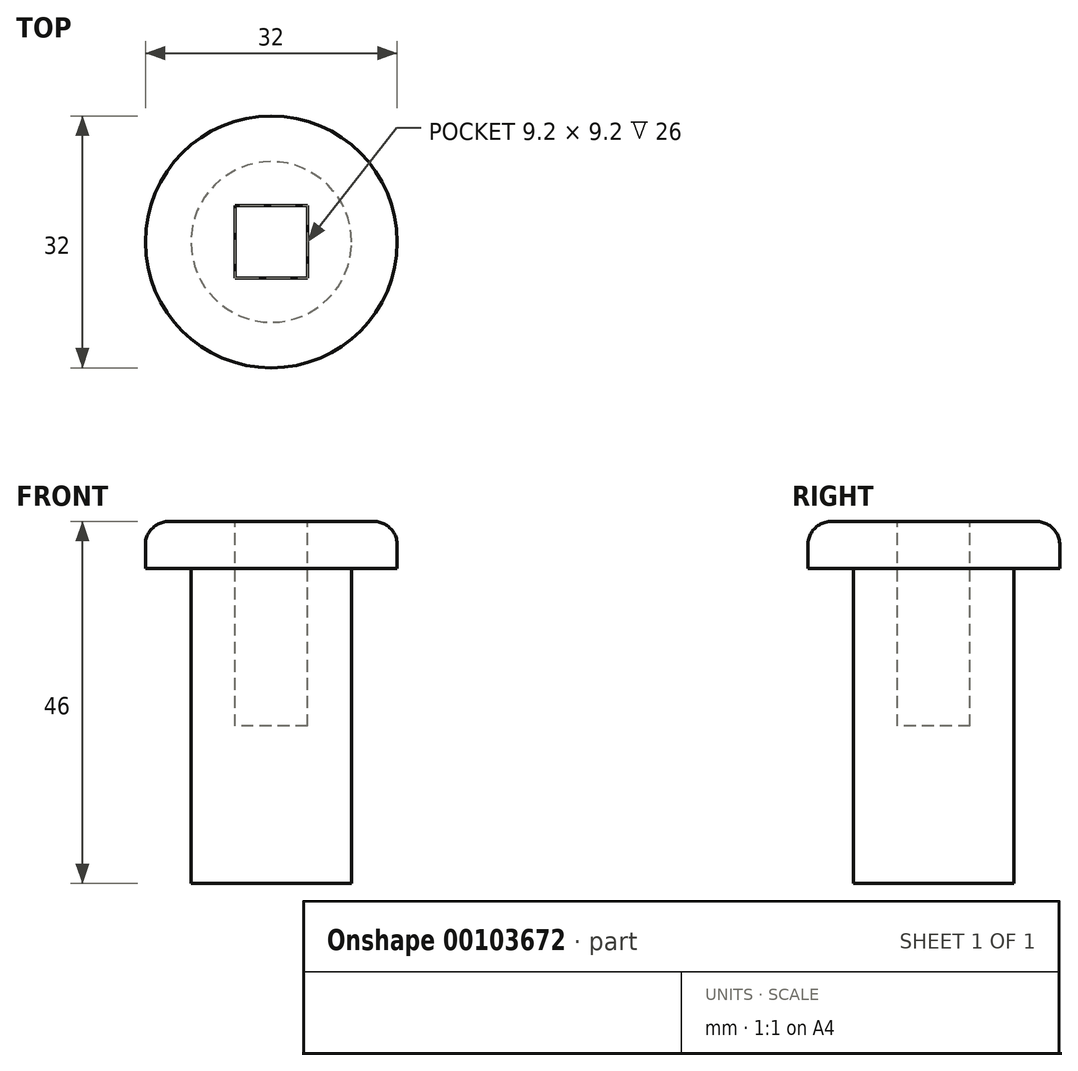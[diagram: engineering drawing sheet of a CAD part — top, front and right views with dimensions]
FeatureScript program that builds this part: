
annotation { "Feature Type Name" : "Feature", "Feature Type Description" : "" }
export const myFeature = defineFeature(function(context is Context, id is Id, definition is map)
    precondition{}
    {
        {
            var Q0;
            Q0=qCreatedBy(makeId("Top.planeOp"),FACE);
            var sketch = newSketch(context, id + "F0", { "sketchPlane" : qUnion([Q0])});
            skCircle(sketch, "E0", {"center": v(0, 0) * mm, "radius": 10.2 * mm});
            skSolve(sketch);
        }
        {
            var Q0;
            Q0=makeQuery(id+"F0.imprint","IMPRINT",FACE,{"disambiguationData":[TD([[makeQuery(id+"F0.imprint","IMPRINT",EDGE,{"derivedFrom":sQuery(id+"F0.wireOp",EDGE,"E0")}),1.0]])]});
            extrude(context, id + "F1", {"entities" : qUnion([Q0]), "depth" : 40 * mm});
        }
        {
            var Q0;
            Q0=makeQuery(id+"F1.opExtrude","CAP_FACE",FACE,{"disambiguationData":[OSD([sQuery(id+"F0.wireOp",EDGE,"E0")])],"isStart":false});
            var sketch = newSketch(context, id + "F2", { "sketchPlane" : qUnion([Q0])});
            skLineSegment(sketch, "E1.bottom", {"start": v(4.6, 4.6) * mm, "end": v(-4.6, 4.6) * mm});
            skLineSegment(sketch, "E1.top", {"start": v(4.6, -4.6) * mm, "end": v(-4.6, -4.6) * mm});
            skLineSegment(sketch, "E1.left", {"start": v(4.6, 4.6) * mm, "end": v(4.6, -4.6) * mm});
            skLineSegment(sketch, "E1.right", {"start": v(-4.6, 4.6) * mm, "end": v(-4.6, -4.6) * mm});
            skPoint(sketch, "E1.middle", {"position": v(0, 0) * mm});
            skSolve(sketch);
        }
        {
            var Q0;
            Q0=makeQuery(id+"F2.imprint","IMPRINT",FACE,{"disambiguationData":[TD([[makeQuery(id+"F2.imprint","IMPRINT",EDGE,{"derivedFrom":sQuery(id+"F2.wireOp",EDGE,"E1.bottom")}),1.0]])]});
            extrude(context, id + "F3", {"entities" : qUnion([Q0]), "operationType" : NewBodyOperationType.REMOVE, "oppositeDirection" : true, "depth" : 20 * mm});
        }
        {
            var Q0;
            Q0=makeQuery(id+"F1.opExtrude","CAP_FACE",FACE,{"disambiguationData":[OSD([sQuery(id+"F0.wireOp",EDGE,"E0")])],"isStart":false});
            var sketch = newSketch(context, id + "F4", { "sketchPlane" : qUnion([Q0])});
            skCircle(sketch, "E2", {"center": v(0, 0) * mm, "radius": 16 * mm});
            skSolve(sketch);
        }
        {
            var Q0;
            Q0=makeQuery(id+"F4.imprint","IMPRINT",FACE,{"disambiguationData":[TD([[makeQuery(id+"F4.imprint","IMPRINT",EDGE,{"derivedFrom":sQuery(id+"F4.wireOp",EDGE,"E2")}),1.0]])]});
            var Q1;
            Q1=makeQuery(id+"F4.imprint","IMPRINT",FACE,{"disambiguationData":[TD([[makeQuery(id+"F4.imprint","IMPRINT",EDGE,{"derivedFrom":makeQuery(id+"F1.opExtrude","CAP_EDGE",EDGE,{"disambiguationData":[OSD([sQuery(id+"F0.wireOp",EDGE,"E0")])],"isStart":false})}),1.0]])]});
            extrude(context, id + "F5", {"entities" : qUnion([Q0, Q1]), "operationType" : NewBodyOperationType.ADD, "depth" : 6 * mm});
        }
        {
            var Q0;
            Q0=makeQuery(id+"F5.opExtrude","CAP_EDGE",EDGE,{"disambiguationData":[OSD([sQuery(id+"F4.wireOp",EDGE,"E2")])],"isStart":false});
            fillet(context, id + "F6", {"entities" : qUnion([Q0]), "radius" : 3 * mm, "tangentPropagation" : true, "allowEdgeOverflow" : false});
        }
    });
